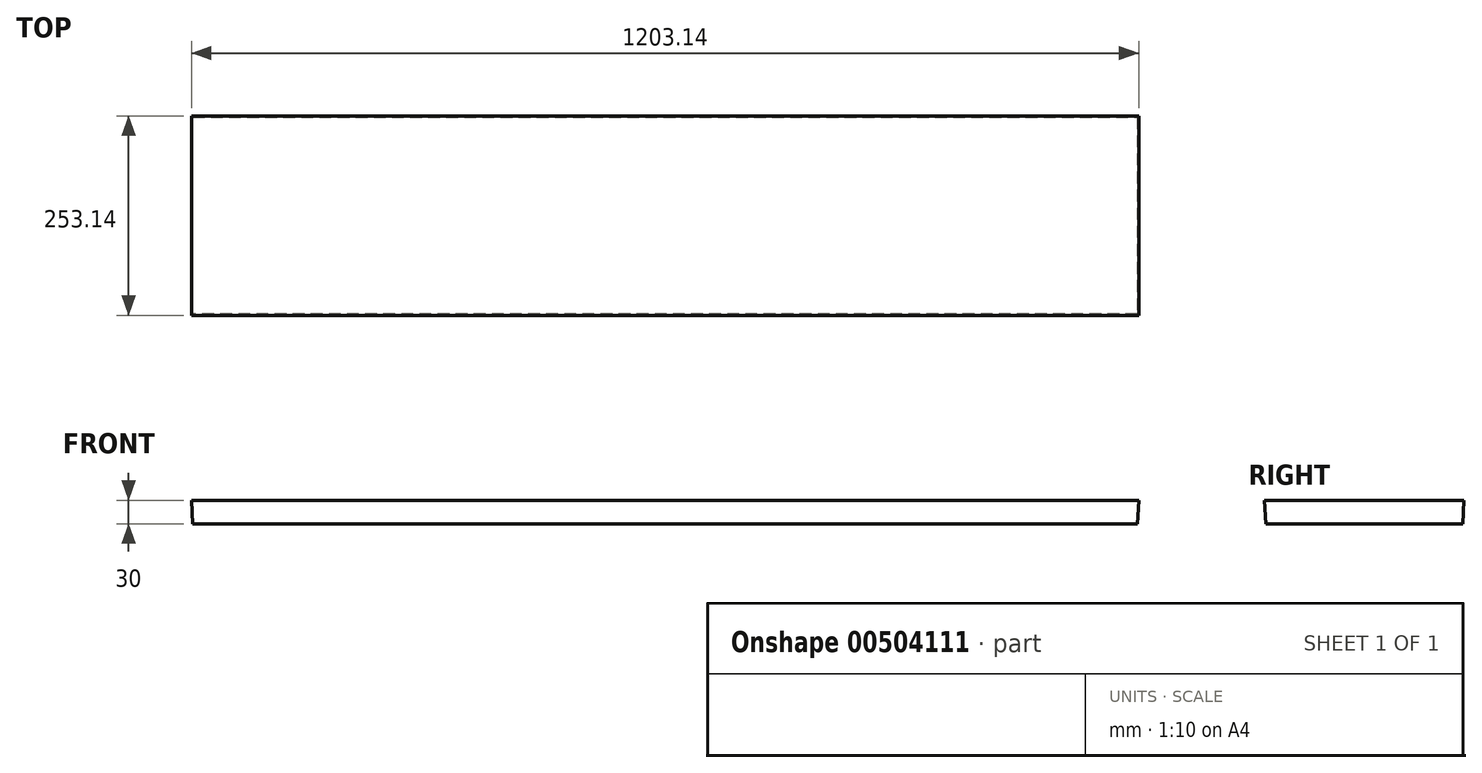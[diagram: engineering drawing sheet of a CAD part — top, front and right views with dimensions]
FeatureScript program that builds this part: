
annotation { "Feature Type Name" : "Feature", "Feature Type Description" : "" }
export const myFeature = defineFeature(function(context is Context, id is Id, definition is map)
    precondition{}
    {
        {
            var Q0;
            Q0=qCreatedBy(makeId("Top.planeOp"),FACE);
            var sketch = newSketch(context, id + "F0", { "sketchPlane" : qUnion([Q0])});
            skLineSegment(sketch, "E0.bottom", {"start": v(0, 0) * mm, "end": v(1200, 0) * mm});
            skLineSegment(sketch, "E0.top", {"start": v(0, -250) * mm, "end": v(1200, -250) * mm});
            skLineSegment(sketch, "E0.left", {"start": v(0, 0) * mm, "end": v(0, -250) * mm});
            skLineSegment(sketch, "E0.right", {"start": v(1200, 0) * mm, "end": v(1200, -250) * mm});
            skSolve(sketch);
        }
        {
            var Q0;
            Q0 = qSketchRegion(id + "F0", true);
            extrude(context, id + "F1", {"entities" : qUnion([Q0]), "depth" : 30 * mm, "offsetDistance" : 25 * mm, "hasDraft" : true, "draftAngle" : 3 * degree});
        }
    });
